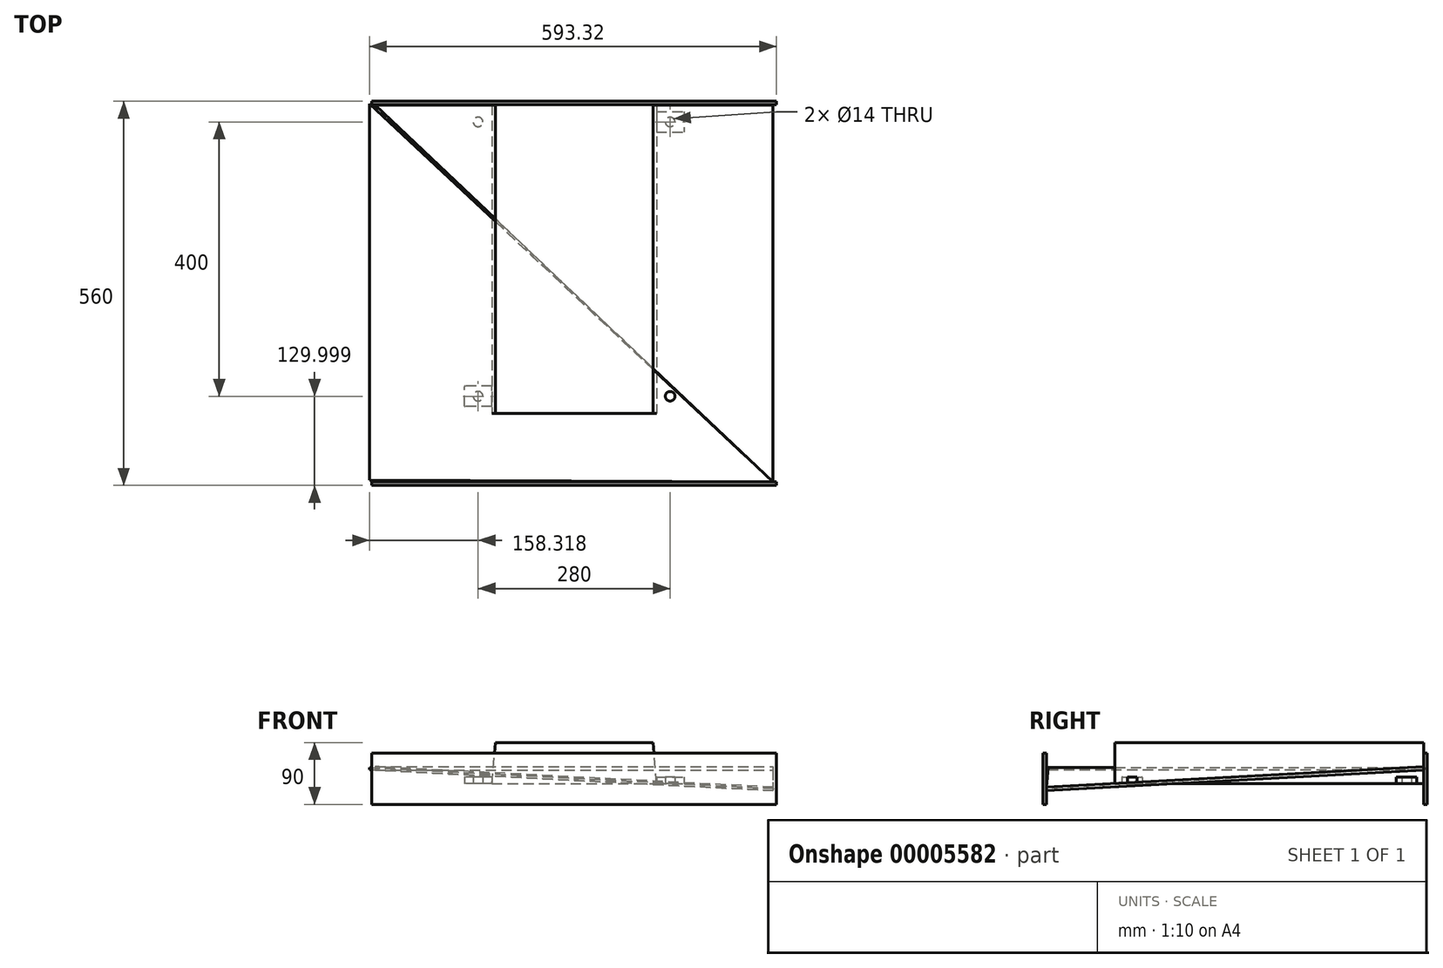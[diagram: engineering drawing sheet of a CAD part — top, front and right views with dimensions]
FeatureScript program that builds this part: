
annotation { "Feature Type Name" : "Feature", "Feature Type Description" : "" }
export const myFeature = defineFeature(function(context is Context, id is Id, definition is map)
    precondition{}
    {
        {
            var Q0;
            Q0=qCreatedBy(makeId("Top.planeOp"),FACE);
            var sketch = newSketch(context, id + "F0", { "sketchPlane" : qUnion([Q0])});
            skLineSegment(sketch, "E0.bottom", {"start": v(44.6, 431.49) * mm, "end": v(284.6, 431.49) * mm});
            skLineSegment(sketch, "E0.top", {"start": v(44.6, -18.51) * mm, "end": v(284.6, -18.51) * mm});
            skLineSegment(sketch, "E0.left", {"start": v(44.6, 431.49) * mm, "end": v(44.6, -18.51) * mm});
            skLineSegment(sketch, "E0.right", {"start": v(284.6, 431.49) * mm, "end": v(284.6, -18.51) * mm});
            skLineSegment(sketch, "E1", {"start": v(164.6, 431.49) * mm, "end": v(164.6, -18.51) * mm, "construction": true});
            skLineSegment(sketch, "E2", {"start": v(284.6, 206.49) * mm, "end": v(44.6, 206.49) * mm, "construction": true});
            skSolve(sketch);
        }
        {
            var Q0;
            Q0=qCreatedBy(makeId("Top.planeOp"),FACE);
            cPlane(context, id + "F1", {"entities" : qUnion([Q0]), "cplaneType" : CPlaneType.OFFSET, "offset" : 60 * mm, "width" : 150 * mm, "height" : 150 * mm});
        }
        {
            var Q0;
            Q0=qCreatedBy(id+"F1.planeOp",FACE);
            var sketch = newSketch(context, id + "F2", { "sketchPlane" : qUnion([Q0])});
            skLineSegment(sketch, "E3.bottom", {"start": v(0, 431.49) * mm, "end": v(329.2, 431.49) * mm});
            skLineSegment(sketch, "E3.top", {"start": v(49.6, -18.51) * mm, "end": v(279.6, -18.51) * mm});
            skLineSegment(sketch, "E3.left", {"start": v(49.6, 431.49) * mm, "end": v(49.6, -18.51) * mm});
            skLineSegment(sketch, "E3.right", {"start": v(279.6, 431.49) * mm, "end": v(279.6, -18.51) * mm});
            skSolve(sketch);
        }
        {
            var Q0;
            Q0=makeQuery(id+"F0.imprint","IMPRINT",FACE,{"disambiguationData":[TD([[makeQuery(id+"F0.imprint","IMPRINT",EDGE,{"derivedFrom":sQuery(id+"F0.wireOp",EDGE,"E0.bottom")}),-1.0]])]});
            var Q1;
            Q1=makeQuery(id+"F2.imprint","IMPRINT",FACE,{"disambiguationData":[TD([[makeQuery(id+"F2.imprint","IMPRINT",EDGE,{"derivedFrom":sQuery(id+"F2.wireOp",EDGE,"E3.top")}),1.0]])]});
            loft(context, id + "F3", {"sheetProfilesArray" : [{ "sheetProfileEntities" : qUnion([Q0]) }, { "sheetProfileEntities" : qUnion([Q1]) }]});
        }
        {
            var Q0;
            Q0=qCreatedBy(makeId("Top.planeOp"),FACE);
            var sketch = newSketch(context, id + "F4", { "sketchPlane" : qUnion([Q0])});
            skLineSegment(sketch, "E4.bottom", {"start": v(44.6, -8.51) * mm, "end": v(4.6, -8.51) * mm});
            skLineSegment(sketch, "E4.top", {"start": v(44.6, 21.49) * mm, "end": v(4.6, 21.49) * mm});
            skLineSegment(sketch, "E4.left", {"start": v(44.6, -8.51) * mm, "end": v(44.6, 21.49) * mm});
            skLineSegment(sketch, "E4.right", {"start": v(4.6, -8.51) * mm, "end": v(4.6, 21.49) * mm});
            skLineSegment(sketch, "E5", {"start": v(44.6, 6.49) * mm, "end": v(4.6, 6.49) * mm, "construction": true});
            skCircle(sketch, "E6", {"center": v(24.6, 6.49) * mm, "radius": 7 * mm});
            skCircle(sketch, "E7.0.MirrorC", {"center": v(304.6, 6.49) * mm, "radius": 7 * mm});
            skLineSegment(sketch, "E8.0.MirrorCS", {"start": v(284.6, -8.51) * mm, "end": v(324.6, -8.51) * mm});
            skLineSegment(sketch, "E9.0.MirrorCS", {"start": v(284.6, -8.51) * mm, "end": v(284.6, 21.49) * mm});
            skLineSegment(sketch, "E10.0.MirrorCS", {"start": v(284.6, 21.49) * mm, "end": v(324.6, 21.49) * mm});
            skLineSegment(sketch, "E11.0.MirrorCS", {"start": v(324.6, -8.51) * mm, "end": v(324.6, 21.49) * mm});
            skCircle(sketch, "E12.0.MirrorC", {"center": v(304.6, 406.49) * mm, "radius": 7 * mm});
            skLineSegment(sketch, "E12.1.MirrorCS", {"start": v(284.6, 421.49) * mm, "end": v(284.6, 391.49) * mm});
            skLineSegment(sketch, "E12.2.MirrorCS", {"start": v(284.6, 421.49) * mm, "end": v(324.6, 421.49) * mm});
            skLineSegment(sketch, "E12.3.MirrorCS", {"start": v(324.6, 421.49) * mm, "end": v(324.6, 391.49) * mm});
            skLineSegment(sketch, "E12.4.MirrorCS", {"start": v(284.6, 391.49) * mm, "end": v(324.6, 391.49) * mm});
            skLineSegment(sketch, "E13.0.MirrorCS", {"start": v(44.6, 406.49) * mm, "end": v(4.6, 406.49) * mm, "construction": true});
            skCircle(sketch, "E13.1.MirrorC", {"center": v(24.6, 406.49) * mm, "radius": 7 * mm});
            skLineSegment(sketch, "E13.2.MirrorCS", {"start": v(44.6, 421.49) * mm, "end": v(44.6, 391.49) * mm});
            skLineSegment(sketch, "E13.3.MirrorCS", {"start": v(4.6, 421.49) * mm, "end": v(4.6, 391.49) * mm});
            skLineSegment(sketch, "E13.4.MirrorCS", {"start": v(44.6, 421.49) * mm, "end": v(4.6, 421.49) * mm});
            skLineSegment(sketch, "E13.5.MirrorCS", {"start": v(44.6, 391.49) * mm, "end": v(4.6, 391.49) * mm});
            skSolve(sketch);
        }
        {
            var Q0;
            {Q0=qUnion([makeQuery(id+"F4.imprint","IMPRINT",FACE,{"disambiguationData":[TD([[makeQuery(id+"F4.imprint","IMPRINT",EDGE,{"derivedFrom":sQuery(id+"F4.wireOp",EDGE,"E4.bottom")}),-1.0]])]}),makeQuery(id+"F4.imprint","IMPRINT",FACE,{"disambiguationData":[TD([[makeQuery(id+"F4.imprint","IMPRINT",EDGE,{"derivedFrom":sQuery(id+"F4.wireOp",EDGE,"E7.0.MirrorC")}),1.0]])]}),makeQuery(id+"F4.imprint","IMPRINT",FACE,{"disambiguationData":[TD([[makeQuery(id+"F4.imprint","IMPRINT",EDGE,{"derivedFrom":sQuery(id+"F4.wireOp",EDGE,"E12.0.MirrorC")}),-1.0]])]}),makeQuery(id+"F4.imprint","IMPRINT",FACE,{"disambiguationData":[TD([[makeQuery(id+"F4.imprint","IMPRINT",EDGE,{"derivedFrom":sQuery(id+"F4.wireOp",EDGE,"E13.1.MirrorC")}),1.0]])]})]);}
            extrude(context, id + "F5", {"entities" : qUnion([Q0]), "depth" : 10 * mm});
        }
        {
            var Q0;
            Q0=makeQuery(id+"F5.opExtrude","SWEPT_EDGE",EDGE,{"disambiguationData":[OSD([sQuery(id+"F4.wireOp",EDGE,"E4.bottom"),sQuery(id+"F4.wireOp",EDGE,"E4.right")])]});
            var Q1;
            Q1=makeQuery(id+"F5.opExtrude","CAP_EDGE",EDGE,{"disambiguationData":[OSD([sQuery(id+"F4.wireOp",EDGE,"E4.bottom")])],"isStart":false});
            var Q2;
            Q2=makeQuery(id+"F5.opExtrude","CAP_EDGE",EDGE,{"disambiguationData":[OSD([sQuery(id+"F4.wireOp",EDGE,"E4.right")])],"isStart":false});
            var Q3;
            Q3=makeQuery(id+"F5.opExtrude","CAP_EDGE",EDGE,{"disambiguationData":[OSD([sQuery(id+"F4.wireOp",EDGE,"E4.top")])],"isStart":false});
            var Q4;
            Q4=makeQuery(id+"F5.opExtrude","SWEPT_EDGE",EDGE,{"disambiguationData":[OSD([sQuery(id+"F4.wireOp",EDGE,"E4.top"),sQuery(id+"F4.wireOp",EDGE,"E4.right")])]});
            fillet(context, id + "F6", {"entities" : qUnion([Q0, Q1, Q2, Q3, Q4]), "radius" : 1 * mm, "tangentPropagation" : true, "allowEdgeOverflow" : false});
        }
        {
            var Q0;
            Q0=qCreatedBy(makeId("Top.planeOp"),FACE);
            cPlane(context, id + "F7", {"entities" : qUnion([Q0]), "cplaneType" : CPlaneType.OFFSET, "offset" : 30 * mm, "oppositeDirection" : true, "width" : 150 * mm, "height" : 150 * mm});
        }
        {
            var Q0;
            Q0=qCreatedBy(id+"F7.planeOp",FACE);
            var sketch = newSketch(context, id + "F8", { "sketchPlane" : qUnion([Q0])});
            skLineSegment(sketch, "E14.bottom", {"start": v(-125.4, 431.49) * mm, "end": v(454.6, 431.49) * mm, "construction": true});
            skLineSegment(sketch, "E14.top", {"start": v(-125.4, -118.51) * mm, "end": v(454.6, -118.51) * mm, "construction": true});
            skLineSegment(sketch, "E14.left", {"start": v(-125.4, 431.49) * mm, "end": v(-125.4, -118.51) * mm, "construction": true});
            skLineSegment(sketch, "E14.right", {"start": v(454.6, 431.49) * mm, "end": v(454.6, -118.51) * mm, "construction": true});
            skLineSegment(sketch, "E15", {"start": v(164.6, -118.51) * mm, "end": v(164.6, 431.49) * mm, "construction": true});
            skLineSegment(sketch, "E16.bottom", {"start": v(-130.4, -118.51) * mm, "end": v(459.6, -118.51) * mm, "construction": true});
            skLineSegment(sketch, "E16.top", {"start": v(-130.4, -123.51) * mm, "end": v(459.6, -123.51) * mm});
            skLineSegment(sketch, "E16.left", {"start": v(-130.4, -118.51) * mm, "end": v(-130.4, -123.51) * mm});
            skLineSegment(sketch, "E16.right", {"start": v(459.6, -118.51) * mm, "end": v(459.6, -123.51) * mm});
            skLineSegment(sketch, "E17", {"start": v(164.6, -123.51) * mm, "end": v(164.6, -118.51) * mm, "construction": true});
            skLineSegment(sketch, "E18.bottom", {"start": v(-130.4, 436.49) * mm, "end": v(459.6, 436.49) * mm});
            skLineSegment(sketch, "E18.top", {"start": v(-130.4, 431.49) * mm, "end": v(459.6, 431.49) * mm});
            skLineSegment(sketch, "E18.left", {"start": v(-130.4, 436.49) * mm, "end": v(-130.4, 431.49) * mm});
            skLineSegment(sketch, "E18.right", {"start": v(459.6, 436.49) * mm, "end": v(459.6, 431.49) * mm});
            skLineSegment(sketch, "E19", {"start": v(164.6, 431.49) * mm, "end": v(164.6, 436.49) * mm, "construction": true});
            skLineSegment(sketch, "E20", {"start": v(-125.4, 431.49) * mm, "end": v(-130.4, 431.49) * mm, "construction": true});
            skLineSegment(sketch, "E21", {"start": v(454.6, 431.49) * mm, "end": v(459.6, 431.49) * mm, "construction": true});
            skLineSegment(sketch, "E22.bottom", {"start": v(-130.4, 431.49) * mm, "end": v(-125.4, 431.49) * mm});
            skLineSegment(sketch, "E22.top", {"start": v(-130.4, -118.51) * mm, "end": v(-125.4, -118.51) * mm});
            skLineSegment(sketch, "E22.left", {"start": v(-130.4, 431.49) * mm, "end": v(-130.4, -118.51) * mm});
            skLineSegment(sketch, "E22.right", {"start": v(-125.4, 431.49) * mm, "end": v(-125.4, -118.51) * mm});
            skLineSegment(sketch, "E23", {"start": v(459.6, -118.51) * mm, "end": v(-130.4, -118.51) * mm});
            skLineSegment(sketch, "E24.bottom", {"start": v(454.6, 431.49) * mm, "end": v(459.6, 431.49) * mm});
            skLineSegment(sketch, "E24.top", {"start": v(454.6, -118.51) * mm, "end": v(459.6, -118.51) * mm});
            skLineSegment(sketch, "E24.left", {"start": v(454.6, 431.49) * mm, "end": v(454.6, -118.51) * mm});
            skLineSegment(sketch, "E24.right", {"start": v(459.6, 431.49) * mm, "end": v(459.6, -118.51) * mm});
            skSolve(sketch);
        }
        {
            var Q0;
            {var subQ9=makeQuery(id+"F8.imprint","IMPRINT",EDGE,{"derivedFrom":sQuery(id+"F8.wireOp",EDGE,"E24.bottom")});var subQ10=makeQuery(id+"F8.imprint","IMPRINT",EDGE,{"derivedFrom":sQuery(id+"F8.wireOp",EDGE,"E22.bottom")});Q0=qUnion([makeQuery(id+"F8.imprint","IMPRINT",FACE,{"disambiguationData":[TD([[makeQuery(id+"F8.imprint","IMPRINT",EDGE,{"derivedFrom":sQuery(id+"F8.wireOp",EDGE,"E16.top")}),1.0]])]}),makeQuery(id+"F8.imprint","IMPRINT",FACE,{"disambiguationData":[TD([[makeQuery(id+"F8.imprint","IMPRINT",EDGE,{"derivedFrom":sQuery(id+"F8.wireOp",EDGE,"E18.bottom")}),-1.0]])]}),makeQuery(id+"F8.imprint","IMPRINT",FACE,{"disambiguationData":[TD([[subQ10,-1.0]])]}),makeQuery(id+"F8.imprint","IMPRINT",FACE,{"disambiguationData":[TD([[subQ9,-1.0]])]})]);}
            extrude(context, id + "F9", {"entities" : qUnion([Q0]), "operationType" : NewBodyOperationType.ADD, "depth" : 75 * mm});
        }
        {
            var Q0;
            Q0=makeQuery(id+"F9.opExtrude","SWEPT_FACE",FACE,{"disambiguationData":[OSD([sQuery(id+"F8.wireOp",EDGE,"E18.top")])]});
            var sketch = newSketch(context, id + "F10", { "sketchPlane" : qUnion([Q0])});
            skLineSegment(sketch, "E25", {"start": v(-125.4, -30) * mm, "end": v(-125.4, 20) * mm, "construction": true});
            skLineSegment(sketch, "E26", {"start": v(454.6, -30) * mm, "end": v(454.6, 20) * mm, "construction": true});
            skSolve(sketch);
        }
        {
            var Q0;
            Q0=makeQuery(id+"F9.opExtrude","SWEPT_FACE",FACE,{"disambiguationData":[OSD([sQuery(id+"F8.wireOp",EDGE,"E23")])]});
            var sketch = newSketch(context, id + "F11", { "sketchPlane" : qUnion([Q0])});
            skLineSegment(sketch, "E27", {"start": v(125.4, -30) * mm, "end": v(125.4, 20) * mm, "construction": true});
            skLineSegment(sketch, "E28", {"start": v(-454.6, -30) * mm, "end": v(-454.6, -10) * mm, "construction": true});
            skSolve(sketch);
        }
        {
            var Q0;
            Q0=sQuery(id+"F10.wireOp",VERTEX,"E25.end");
            var Q1;
            Q1=sQuery(id+"F11.wireOp",VERTEX,"E27.end");
            var Q2;
            Q2=sQuery(id+"F11.wireOp",VERTEX,"E28.end");
            cPlane(context, id + "F12", {"entities" : qUnion([Q0, Q1, Q2]), "cplaneType" : CPlaneType.THREE_POINT, "offset" : 150 * mm, "width" : 150 * mm, "height" : 150 * mm});
        }
        {
            var Q0;
            Q0=qCreatedBy(id+"F12.planeOp",FACE);
            var sketch = newSketch(context, id + "F13", { "sketchPlane" : qUnion([Q0])});
            skLineSegment(sketch, "E29", {"start": v(-134.6, 115.97) * mm, "end": v(-134.6, -433.15) * mm});
            skLineSegment(sketch, "E30", {"start": v(-134.6, -433.15) * mm, "end": v(454.5, 118.51) * mm});
            skLineSegment(sketch, "E31", {"start": v(454.5, 118.51) * mm, "end": v(-134.6, 115.97) * mm});
            skSolve(sketch);
        }
        {
            var Q0;
            Q0=makeQuery(id+"F13.imprint","IMPRINT",FACE,{"disambiguationData":[TD([[makeQuery(id+"F13.imprint","IMPRINT",EDGE,{"derivedFrom":sQuery(id+"F13.wireOp",EDGE,"E29")}),1.0]])]});
            extrude(context, id + "F14", {"entities" : qUnion([Q0]), "oppositeDirection" : true, "depth" : 3 * mm});
        }
        {
            var Q0;
            Q0=sQuery(id+"F10.wireOp",VERTEX,"E26.end");
            var Q1;
            Q1=sQuery(id+"F11.wireOp",VERTEX,"E28.end");
            var Q2;
            Q2=sQuery(id+"F10.wireOp",VERTEX,"E25.end");
            cPlane(context, id + "F15", {"entities" : qUnion([Q0, Q1, Q2]), "cplaneType" : CPlaneType.THREE_POINT, "offset" : 150 * mm, "width" : 150 * mm, "height" : 150 * mm});
        }
        {
            var Q0;
            Q0=qCreatedBy(id+"F15.planeOp",FACE);
            var sketch = newSketch(context, id + "F16", { "sketchPlane" : qUnion([Q0])});
            skLineSegment(sketch, "E32", {"start": v(-125.4, 431.94) * mm, "end": v(454.6, 431.94) * mm});
            skLineSegment(sketch, "E33", {"start": v(454.6, 431.94) * mm, "end": v(454.6, -118.88) * mm});
            skLineSegment(sketch, "E34", {"start": v(454.6, -118.88) * mm, "end": v(-125.4, 431.94) * mm});
            skSolve(sketch);
        }
        {
            var Q0;
            Q0=makeQuery(id+"F16.imprint","IMPRINT",FACE,{"disambiguationData":[TD([[makeQuery(id+"F16.imprint","IMPRINT",EDGE,{"derivedFrom":sQuery(id+"F16.wireOp",EDGE,"E32")}),-1.0]])]});
            extrude(context, id + "F17", {"entities" : qUnion([Q0]), "depth" : 5 * mm});
        }
    });
